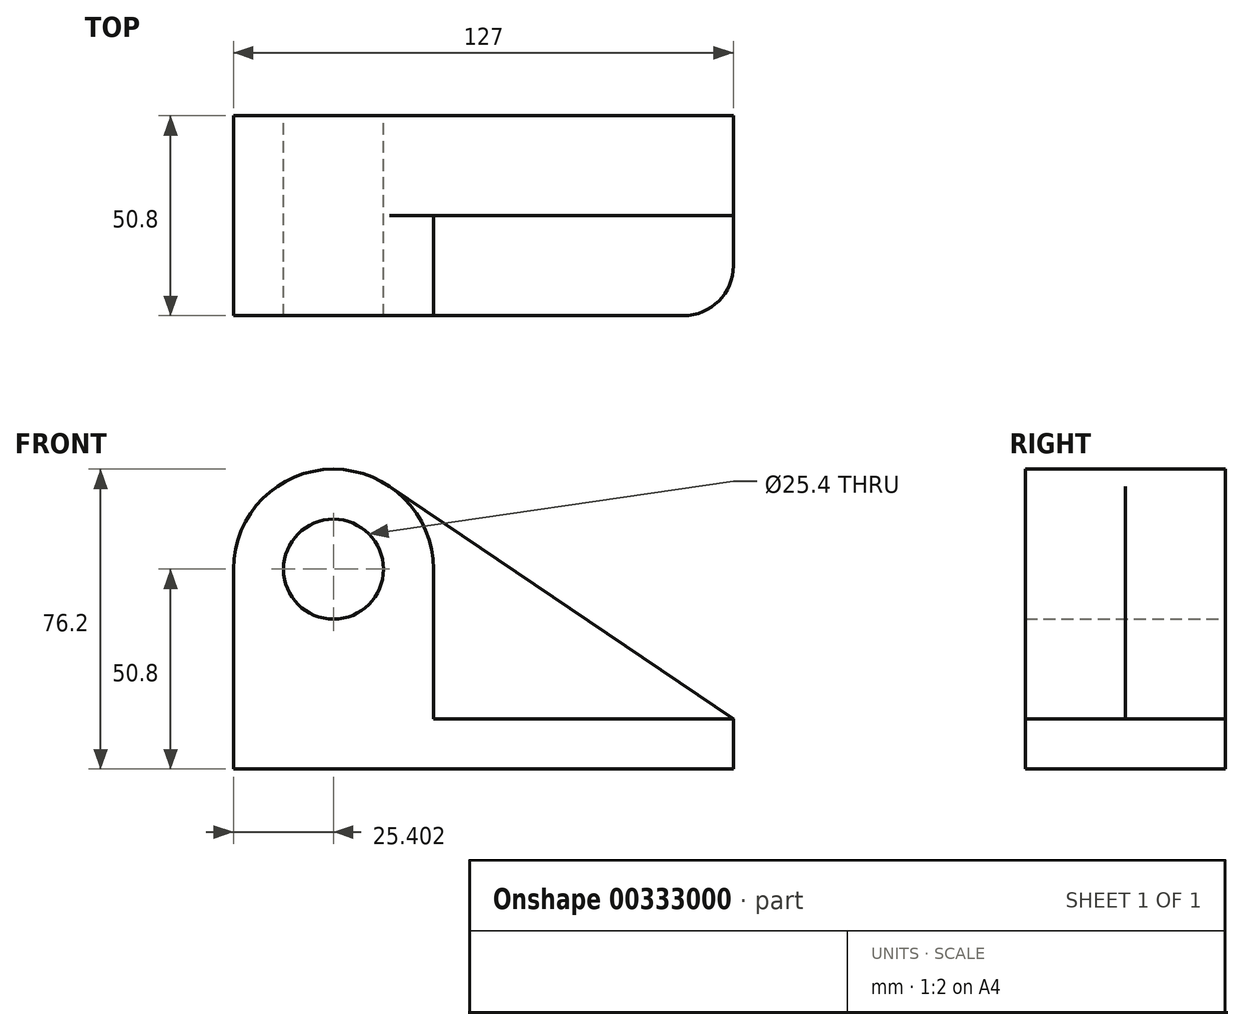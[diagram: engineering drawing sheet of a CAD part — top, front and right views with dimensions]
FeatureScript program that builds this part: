
annotation { "Feature Type Name" : "Feature", "Feature Type Description" : "" }
export const myFeature = defineFeature(function(context is Context, id is Id, definition is map)
    precondition{}
    {
        {
            var Q0;
            Q0=qCreatedBy(makeId("Front.planeOp"),FACE);
            var sketch = newSketch(context, id + "F0", { "sketchPlane" : qUnion([Q0])});
            skCircle(sketch, "E0", {"center": v(-53.93, 38.1) * mm, "radius": 12.7 * mm});
            skArc(sketch, "E1", {"start": v(-39.68, 59.13) * mm, "mid": v(-65.83, 60.54) * mm, "end": v(-79.33, 38.1) * mm});
            skLineSegment(sketch, "E2", {"start": v(-79.33, 38.1) * mm, "end": v(-79.33, -12.7) * mm});
            skLineSegment(sketch, "E3", {"start": v(47.67, -12.7) * mm, "end": v(-79.33, -12.7) * mm});
            skLineSegment(sketch, "E4", {"start": v(47.67, -12.7) * mm, "end": v(47.67, 0) * mm});
            skLineSegment(sketch, "E5", {"start": v(47.67, 0) * mm, "end": v(-39.68, 59.13) * mm});
            skSolve(sketch);
        }
        {
            var Q0;
            Q0=makeQuery(id+"F0.imprint","IMPRINT",FACE,{"disambiguationData":[TD([[makeQuery(id+"F0.imprint","IMPRINT",EDGE,{"derivedFrom":sQuery(id+"F0.wireOp",EDGE,"E0")}),-1.0]])]});
            extrude(context, id + "F1", {"entities" : qUnion([Q0]), "depth" : 25.4 * mm});
        }
        {
            var Q0;
            Q0=makeQuery(id+"F1.opExtrude","CAP_FACE",FACE,{"disambiguationData":[OSD([sQuery(id+"F0.wireOp",EDGE,"E0"),sQuery(id+"F0.wireOp",EDGE,"E1"),sQuery(id+"F0.wireOp",EDGE,"E2"),sQuery(id+"F0.wireOp",EDGE,"E3"),sQuery(id+"F0.wireOp",EDGE,"E4"),sQuery(id+"F0.wireOp",EDGE,"E5")])],"isStart":false});
            var sketch = newSketch(context, id + "F2", { "sketchPlane" : qUnion([Q0])});
            skCircle(sketch, "E6", {"center": v(-53.93, 38.1) * mm, "radius": 12.7 * mm});
            skArc(sketch, "E7", {"start": v(-28.53, 38.1) * mm, "mid": v(-53.93, 63.5) * mm, "end": v(-79.33, 38.1) * mm});
            skLineSegment(sketch, "E8.bottom", {"start": v(47.67, 0) * mm, "end": v(-28.53, 0) * mm});
            skLineSegment(sketch, "E8.top", {"start": v(47.67, -12.7) * mm, "end": v(-79.33, -12.7) * mm});
            skLineSegment(sketch, "E8.left", {"start": v(47.67, 0) * mm, "end": v(47.67, -12.7) * mm});
            skLineSegment(sketch, "E8.right", {"start": v(-79.33, 0) * mm, "end": v(-79.33, -12.7) * mm});
            skLineSegment(sketch, "E9", {"start": v(-53.93, 38.1) * mm, "end": v(-79.33, 38.1) * mm});
            skLineSegment(sketch, "E10", {"start": v(-79.33, 38.1) * mm, "end": v(-53.93, 38.1) * mm});
            skLineSegment(sketch, "E11", {"start": v(-28.53, 38.1) * mm, "end": v(-53.93, 38.1) * mm});
            skLineSegment(sketch, "E12", {"start": v(-79.33, 38.1) * mm, "end": v(-79.33, 0) * mm});
            skLineSegment(sketch, "E13", {"start": v(-28.53, 38.1) * mm, "end": v(-28.53, 0) * mm});
            skSolve(sketch);
        }
        {
            var Q0;
            Q0=makeQuery(id+"F2.imprint","IMPRINT",FACE,{"disambiguationData":[TD([[makeQuery(id+"F2.imprint","IMPRINT",EDGE,{"derivedFrom":sQuery(id+"F2.wireOp",EDGE,"E8.bottom")}),1.0]])]});
            var Q1;
            {var subQ0=sQuery(id+"F2.wireOp",EDGE,"E10");var subQ3=sQuery(id+"F2.wireOp",EDGE,"E6");var subQ4=makeQuery(id+"F2.imprint","INTERSECT",VERTEX,{"derivedFrom":[subQ3,subQ0]});Q1=makeQuery(id+"F2.imprint","IMPRINT",FACE,{"disambiguationData":[TD([[makeQuery(id+"F2.imprint","IMPRINT",EDGE,{"disambiguationData":[TD([[subQ4,1.0]])],"derivedFrom":subQ3}),-1.0]])]});}
            extrude(context, id + "F3", {"entities" : qUnion([Q0, Q1]), "operationType" : NewBodyOperationType.ADD, "depth" : 25.4 * mm});
        }
        {
            var Q0;
            Q0=makeQuery(id+"F3.opExtrude","CAP_EDGE",EDGE,{"disambiguationData":[OSD([sQuery(id+"F2.wireOp",EDGE,"E8.left")])],"isStart":false});
            fillet(context, id + "F4", {"entities" : qUnion([Q0]), "radius" : 12.7 * mm, "tangentPropagation" : true, "allowEdgeOverflow" : false});
        }
    });
